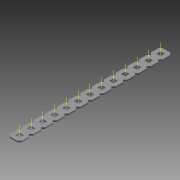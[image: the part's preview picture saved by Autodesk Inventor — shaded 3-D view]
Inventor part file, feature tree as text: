
AUTODESK INVENTOR PART (.ipt)
format: ipt  version: 2015 (Build 190159000, 159)  size: 1,148,416 bytes
history: native  units: in
note: dims shown in document units (in); Inventor stores cm internally (conversion verified against a paired STEP export)
features: other x22, extrude x2, pattern_linear x1, imported_body x1
ambient origin geometry x8: Origin, YZ Plane, XZ Plane, XY Plane, X Axis, Y Axis, Z Axis, Center Point
bodies: Body1 (feature_tree)
feature tree (26):
  other  "Diamond-Pattern"
  other  "Plate"
  extrude  "length cut"  TaperAngle=0.0deg  [1 undecoded]
  extrude  "width cut"  TaperAngle=0.0deg  [1 undecoded]
  other  "constraint axis"
  pattern_linear  "constraint axes"  Spacing1=0.5in  [1 undecoded]
  other  "front plane"
  other  "right plane"
  imported_body  "Base1"
  other  "length profile"
  other  "width profile"
  other  "Work Point1"
  other  "back plane"
  other  "left plane"
  other  "Work Axis170"
  other  "Work Axis171"
  other  "Work Axis172"
  other  "Work Axis173"
  other  "Work Axis174"
  other  "Work Axis175"
  other  "Work Axis176"
  other  "Work Axis177"
  other  "Work Axis178"
  other  "Work Axis179"
  other  "Work Axis180"
  other  "Work Axis181"
note: 3 required parameter values undecoded (feature->parameter linkage not recoverable at this tier; creation-order binding heuristic only, values carry confidence <= 0.55)
